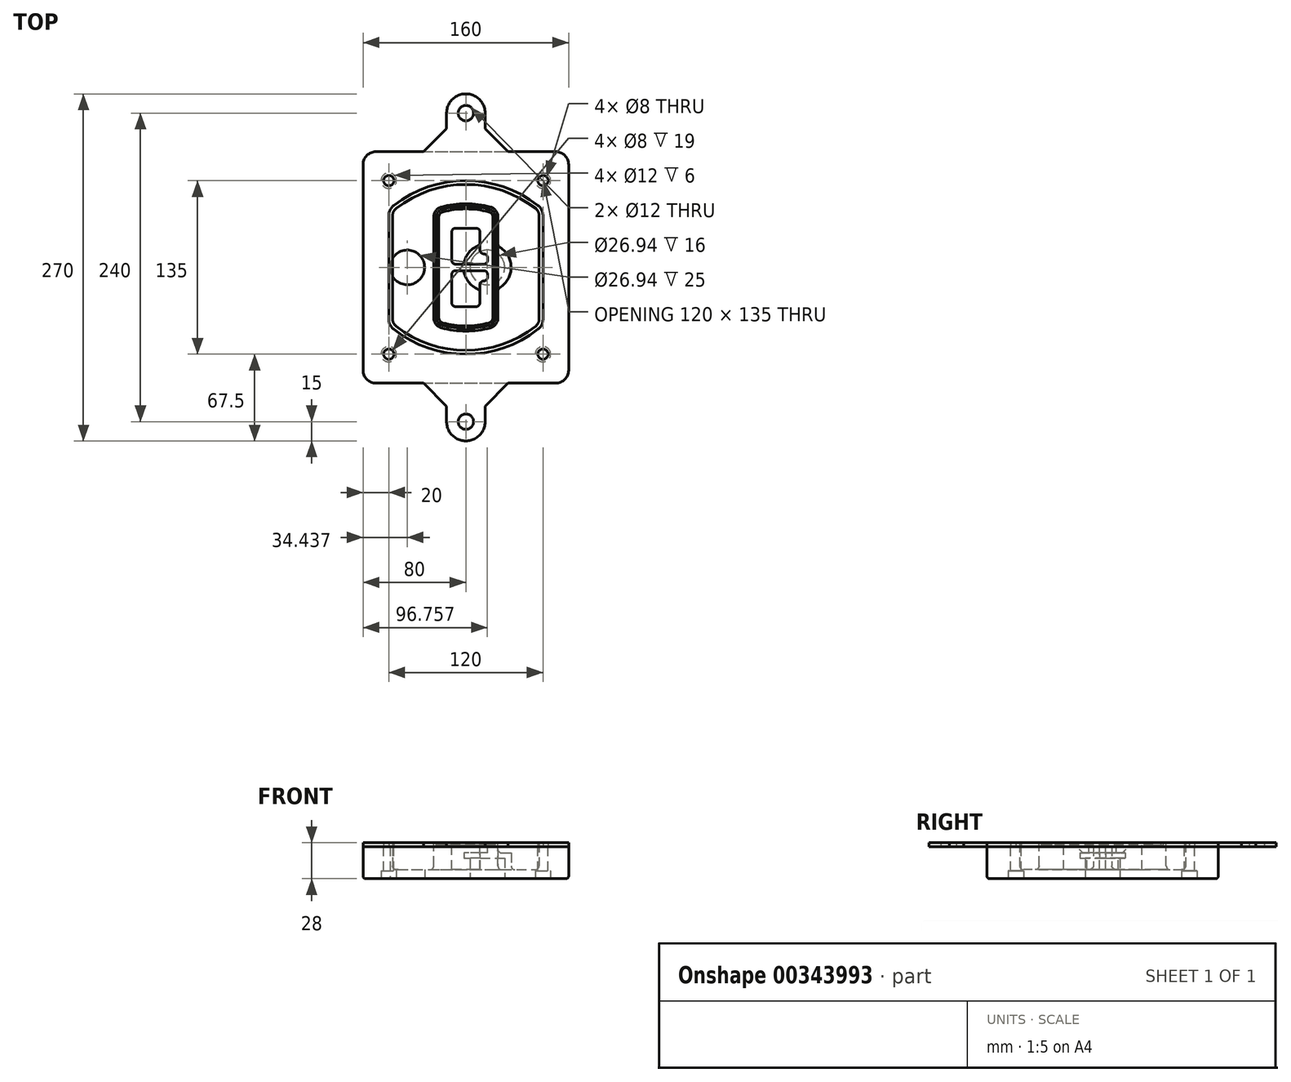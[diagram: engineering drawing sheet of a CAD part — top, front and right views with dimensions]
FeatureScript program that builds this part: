
annotation { "Feature Type Name" : "Feature", "Feature Type Description" : "" }
export const myFeature = defineFeature(function(context is Context, id is Id, definition is map)
    precondition{}
    {
        {
            var Q0;
            Q0=qCreatedBy(makeId("Top.planeOp"),FACE);
            var sketch = newSketch(context, id + "F0", { "sketchPlane" : qUnion([Q0])});
            skPoint(sketch, "E0.rect.middle", {"position": v(0, 0) * mm});
            skLineSegment(sketch, "E1.bottom", {"start": v(-70, -90) * mm, "end": v(70, -90) * mm});
            skLineSegment(sketch, "E1.top", {"start": v(-70, 90) * mm, "end": v(70, 90) * mm});
            skLineSegment(sketch, "E1.left", {"start": v(-80, -80) * mm, "end": v(-80, 80) * mm});
            skLineSegment(sketch, "E1.right", {"start": v(80, -80) * mm, "end": v(80, 80) * mm});
            skLineSegment(sketch, "E2", {"start": v(-80, 90) * mm, "end": v(80, -90) * mm, "construction": true});
            skLineSegment(sketch, "E3", {"start": v(80, 90) * mm, "end": v(-80, -90) * mm, "construction": true});
            skCircle(sketch, "E4", {"center": v(-60, 67.5) * mm, "radius": 4 * mm});
            skCircle(sketch, "E5", {"center": v(60, 67.5) * mm, "radius": 4 * mm});
            skCircle(sketch, "E6", {"center": v(60, -67.5) * mm, "radius": 4 * mm});
            skCircle(sketch, "E7", {"center": v(-60, -67.5) * mm, "radius": 4 * mm});
            skLineSegment(sketch, "E8", {"start": v(-60, 67.5) * mm, "end": v(60, 67.5) * mm, "construction": true});
            skLineSegment(sketch, "E9", {"start": v(60, 67.5) * mm, "end": v(60, -67.5) * mm, "construction": true});
            skLineSegment(sketch, "E10", {"start": v(60, -67.5) * mm, "end": v(-60, -67.5) * mm, "construction": true});
            skLineSegment(sketch, "E11", {"start": v(-60, -67.5) * mm, "end": v(-60, 67.5) * mm, "construction": true});
            skLineSegment(sketch, "E12", {"start": v(-60, 40.3) * mm, "end": v(-60, -40.3) * mm});
            skLineSegment(sketch, "E13", {"start": v(60, 40.3) * mm, "end": v(60, -40.3) * mm});
            skArc(sketch, "E14", {"start": v(56.15, 48.18) * mm, "mid": v(0, 67.5) * mm, "end": v(-56.15, 48.18) * mm});
            skArc(sketch, "E15", {"start": v(-56.15, -48.18) * mm, "mid": v(0, -67.5) * mm, "end": v(56.15, -48.18) * mm});
            skLineSegment(sketch, "E16", {"start": v(-60, 0) * mm, "end": v(60, 0) * mm, "construction": true});
            skPoint(sketch, "E17.visualSharp", {"position": v(-60, -45) * mm});
            skArc(sketch, "E17.filletArc", {"start": v(-60, -40.3) * mm, "mid": v(-58.99, -44.68) * mm, "end": v(-56.15, -48.18) * mm});
            skPoint(sketch, "E18.visualSharp", {"position": v(-60, 45) * mm});
            skArc(sketch, "E18.filletArc", {"start": v(-56.15, 48.18) * mm, "mid": v(-58.99, 44.68) * mm, "end": v(-60, 40.3) * mm});
            skPoint(sketch, "E19.visualSharp", {"position": v(60, 45) * mm});
            skArc(sketch, "E19.filletArc", {"start": v(60, 40.3) * mm, "mid": v(58.99, 44.68) * mm, "end": v(56.15, 48.18) * mm});
            skPoint(sketch, "E20.visualSharp", {"position": v(60, -45) * mm});
            skArc(sketch, "E20.filletArc", {"start": v(56.15, -48.18) * mm, "mid": v(58.99, -44.68) * mm, "end": v(60, -40.3) * mm});
            skPoint(sketch, "E21.visualSharp", {"position": v(-80, 90) * mm});
            skArc(sketch, "E21.filletArc", {"start": v(-70, 90) * mm, "mid": v(-77.07, 87.07) * mm, "end": v(-80, 80) * mm});
            skPoint(sketch, "E22.visualSharp", {"position": v(80, 90) * mm});
            skArc(sketch, "E22.filletArc", {"start": v(80, 80) * mm, "mid": v(77.07, 87.07) * mm, "end": v(70, 90) * mm});
            skPoint(sketch, "E23.visualSharp", {"position": v(80, -90) * mm});
            skArc(sketch, "E23.filletArc", {"start": v(70, -90) * mm, "mid": v(77.07, -87.07) * mm, "end": v(80, -80) * mm});
            skPoint(sketch, "E24.visualSharp", {"position": v(-80, -90) * mm});
            skArc(sketch, "E24.filletArc", {"start": v(-80, -80) * mm, "mid": v(-77.07, -87.07) * mm, "end": v(-70, -90) * mm});
            skArc(sketch, "E25.0", {"start": v(57, 40.3) * mm, "mid": v(56.3, 43.36) * mm, "end": v(54.3, 45.81) * mm});
            skLineSegment(sketch, "E25.1", {"start": v(57, 40.3) * mm, "end": v(57, -40.3) * mm});
            skArc(sketch, "E25.2", {"start": v(54.3, -45.81) * mm, "mid": v(56.3, -43.36) * mm, "end": v(57, -40.3) * mm});
            skArc(sketch, "E25.3", {"start": v(-54.3, -45.81) * mm, "mid": v(0, -64.5) * mm, "end": v(54.3, -45.81) * mm});
            skArc(sketch, "E25.4", {"start": v(-57, -40.3) * mm, "mid": v(-56.3, -43.36) * mm, "end": v(-54.3, -45.81) * mm});
            skArc(sketch, "E25.5", {"start": v(54.3, 45.81) * mm, "mid": v(0, 64.5) * mm, "end": v(-54.3, 45.81) * mm});
            skLineSegment(sketch, "E25.6", {"start": v(-57, 40.3) * mm, "end": v(-57, -40.3) * mm});
            skArc(sketch, "E25.7", {"start": v(-54.3, 45.81) * mm, "mid": v(-56.3, 43.36) * mm, "end": v(-57, 40.3) * mm});
            skArc(sketch, "E26.0", {"start": v(-58.62, 51.33) * mm, "mid": v(-62.58, 46.43) * mm, "end": v(-64, 40.3) * mm});
            skArc(sketch, "E26.1", {"start": v(58.62, 51.33) * mm, "mid": v(0, 71.5) * mm, "end": v(-58.62, 51.33) * mm});
            skArc(sketch, "E26.2", {"start": v(64, 40.3) * mm, "mid": v(62.58, 46.43) * mm, "end": v(58.62, 51.33) * mm});
            skLineSegment(sketch, "E26.3", {"start": v(64, 40.3) * mm, "end": v(64, -40.3) * mm});
            skArc(sketch, "E26.4", {"start": v(58.62, -51.33) * mm, "mid": v(62.58, -46.43) * mm, "end": v(64, -40.3) * mm});
            skLineSegment(sketch, "E26.5", {"start": v(-64, 40.3) * mm, "end": v(-64, -40.3) * mm});
            skArc(sketch, "E26.6", {"start": v(-58.62, -51.33) * mm, "mid": v(0, -71.5) * mm, "end": v(58.62, -51.33) * mm});
            skArc(sketch, "E26.7", {"start": v(-64, -40.3) * mm, "mid": v(-62.58, -46.43) * mm, "end": v(-58.62, -51.33) * mm});
            skSolve(sketch);
        }
        {
            var Q0;
            Q0=makeQuery(id+"F0.imprint","IMPRINT",FACE,{"disambiguationData":[TD([[makeQuery(id+"F0.imprint","IMPRINT",EDGE,{"derivedFrom":sQuery(id+"F0.wireOp",EDGE,"E1.bottom")}),1.0]])]});
            var Q1;
            Q1=makeQuery(id+"F0.imprint","IMPRINT",FACE,{"disambiguationData":[TD([[makeQuery(id+"F0.imprint","IMPRINT",EDGE,{"derivedFrom":sQuery(id+"F0.wireOp",EDGE,"E12")}),1.0]])]});
            var Q2;
            Q2=makeQuery(id+"F0.imprint","IMPRINT",FACE,{"disambiguationData":[TD([[makeQuery(id+"F0.imprint","IMPRINT",EDGE,{"derivedFrom":sQuery(id+"F0.wireOp",EDGE,"E25.0")}),1.0]])]});
            var Q3;
            Q3=makeQuery(id+"F0.imprint","IMPRINT",FACE,{"disambiguationData":[TD([[makeQuery(id+"F0.imprint","IMPRINT",EDGE,{"derivedFrom":sQuery(id+"F0.wireOp",EDGE,"E12")}),-1.0]])]});
            extrude(context, id + "F1", {"entities" : qUnion([Q0, Q1, Q2, Q3]), "oppositeDirection" : true, "depth" : 25 * mm});
        }
        {
            var Q0;
            Q0=makeQuery(id+"F0.imprint","IMPRINT",FACE,{"disambiguationData":[TD([[makeQuery(id+"F0.imprint","IMPRINT",EDGE,{"derivedFrom":sQuery(id+"F0.wireOp",EDGE,"E12")}),1.0]])]});
            extrude(context, id + "F2", {"entities" : qUnion([Q0]), "operationType" : NewBodyOperationType.ADD, "depth" : 3 * mm});
        }
        {
            var Q0;
            Q0=makeQuery(id+"F0.imprint","IMPRINT",FACE,{"disambiguationData":[TD([[makeQuery(id+"F0.imprint","IMPRINT",EDGE,{"derivedFrom":sQuery(id+"F0.wireOp",EDGE,"E25.0")}),1.0]])]});
            extrude(context, id + "F3", {"entities" : qUnion([Q0]), "operationType" : NewBodyOperationType.REMOVE, "oppositeDirection" : true, "depth" : 18 * mm});
        }
        {
            var Q0;
            Q0=makeQuery(id+"F2.opExtrude","CAP_FACE",FACE,{"disambiguationData":[OSD([sQuery(id+"F0.wireOp",EDGE,"E12"),sQuery(id+"F0.wireOp",EDGE,"E13"),sQuery(id+"F0.wireOp",EDGE,"E14"),sQuery(id+"F0.wireOp",EDGE,"E15"),sQuery(id+"F0.wireOp",EDGE,"E17.filletArc"),sQuery(id+"F0.wireOp",EDGE,"E18.filletArc"),sQuery(id+"F0.wireOp",EDGE,"E19.filletArc"),sQuery(id+"F0.wireOp",EDGE,"E20.filletArc"),sQuery(id+"F0.wireOp",EDGE,"E25.0"),sQuery(id+"F0.wireOp",EDGE,"E25.1"),sQuery(id+"F0.wireOp",EDGE,"E25.2"),sQuery(id+"F0.wireOp",EDGE,"E25.3"),sQuery(id+"F0.wireOp",EDGE,"E25.4"),sQuery(id+"F0.wireOp",EDGE,"E25.5"),sQuery(id+"F0.wireOp",EDGE,"E25.6"),sQuery(id+"F0.wireOp",EDGE,"E25.7")])],"isStart":false});
            var sketch = newSketch(context, id + "F4", { "sketchPlane" : qUnion([Q0])});
            skArc(sketch, "E27.0", {"start": v(-19.08, -46.97) * mm, "mid": v(0, -49.5) * mm, "end": v(19.08, -46.97) * mm});
            skArc(sketch, "E28.0", {"start": v(19.08, 46.97) * mm, "mid": v(0, 49.5) * mm, "end": v(-19.08, 46.97) * mm});
            skLineSegment(sketch, "E29", {"start": v(-25, 39.25) * mm, "end": v(-25, -39.25) * mm});
            skLineSegment(sketch, "E30", {"start": v(25, 39.25) * mm, "end": v(25, -39.25) * mm});
            skLineSegment(sketch, "E31", {"start": v(-25, 45.1) * mm, "end": v(25, 45.1) * mm, "construction": true});
            skLineSegment(sketch, "E32", {"start": v(-25, -45.1) * mm, "end": v(25, -45.1) * mm, "construction": true});
            skPoint(sketch, "E33.visualSharp", {"position": v(-25, 45.1) * mm});
            skArc(sketch, "E33.filletArc", {"start": v(-19.08, 46.97) * mm, "mid": v(-23.35, 44.11) * mm, "end": v(-25, 39.25) * mm});
            skPoint(sketch, "E34.visualSharp", {"position": v(25, 45.1) * mm});
            skArc(sketch, "E34.filletArc", {"start": v(25, 39.25) * mm, "mid": v(23.35, 44.11) * mm, "end": v(19.08, 46.97) * mm});
            skPoint(sketch, "E35.visualSharp", {"position": v(25, -45.1) * mm});
            skArc(sketch, "E35.filletArc", {"start": v(19.08, -46.97) * mm, "mid": v(23.35, -44.11) * mm, "end": v(25, -39.25) * mm});
            skPoint(sketch, "E36.visualSharp", {"position": v(-25, -45.1) * mm});
            skArc(sketch, "E36.filletArc", {"start": v(-25, -39.25) * mm, "mid": v(-23.35, -44.11) * mm, "end": v(-19.08, -46.97) * mm});
            skArc(sketch, "E37.0", {"start": v(54.3, 45.81) * mm, "mid": v(0, 64.5) * mm, "end": v(-54.3, 45.81) * mm});
            skArc(sketch, "E37.1", {"start": v(-54.3, 45.81) * mm, "mid": v(-56.3, 43.36) * mm, "end": v(-57, 40.3) * mm});
            skLineSegment(sketch, "E37.2", {"start": v(-57, 40.3) * mm, "end": v(-57, -40.3) * mm});
            skArc(sketch, "E37.3", {"start": v(-57, -40.3) * mm, "mid": v(-56.3, -43.36) * mm, "end": v(-54.3, -45.81) * mm});
            skArc(sketch, "E37.4", {"start": v(-54.3, -45.81) * mm, "mid": v(0, -64.5) * mm, "end": v(54.3, -45.81) * mm});
            skArc(sketch, "E37.5", {"start": v(54.3, -45.81) * mm, "mid": v(56.3, -43.36) * mm, "end": v(57, -40.3) * mm});
            skLineSegment(sketch, "E37.6", {"start": v(57, 40.3) * mm, "end": v(57, -40.3) * mm});
            skArc(sketch, "E37.7", {"start": v(57, 40.3) * mm, "mid": v(56.3, 43.36) * mm, "end": v(54.3, 45.81) * mm});
            skLineSegment(sketch, "E38.0", {"start": v(23, 39.25) * mm, "end": v(23, -39.25) * mm});
            skArc(sketch, "E38.1", {"start": v(18.56, -45.04) * mm, "mid": v(21.76, -42.9) * mm, "end": v(23, -39.25) * mm});
            skArc(sketch, "E38.2", {"start": v(-18.56, -45.04) * mm, "mid": v(0, -47.5) * mm, "end": v(18.56, -45.04) * mm});
            skArc(sketch, "E38.3", {"start": v(-23, -39.25) * mm, "mid": v(-21.76, -42.9) * mm, "end": v(-18.56, -45.04) * mm});
            skLineSegment(sketch, "E38.4", {"start": v(-23, 39.25) * mm, "end": v(-23, -39.25) * mm});
            skArc(sketch, "E38.5", {"start": v(23, 39.25) * mm, "mid": v(21.76, 42.9) * mm, "end": v(18.56, 45.04) * mm});
            skArc(sketch, "E38.6", {"start": v(-18.56, 45.04) * mm, "mid": v(-21.76, 42.9) * mm, "end": v(-23, 39.25) * mm});
            skArc(sketch, "E38.7", {"start": v(18.56, 45.04) * mm, "mid": v(0, 47.5) * mm, "end": v(-18.56, 45.04) * mm});
            skArc(sketch, "E39.0", {"start": v(21, 39.25) * mm, "mid": v(20.18, 41.68) * mm, "end": v(18.04, 43.1) * mm});
            skLineSegment(sketch, "E39.1", {"start": v(21, 39.25) * mm, "end": v(21, -39.25) * mm});
            skArc(sketch, "E39.2", {"start": v(18.04, -43.1) * mm, "mid": v(20.18, -41.68) * mm, "end": v(21, -39.25) * mm});
            skArc(sketch, "E39.3", {"start": v(-18.04, -43.1) * mm, "mid": v(0, -45.5) * mm, "end": v(18.04, -43.1) * mm});
            skArc(sketch, "E39.4", {"start": v(-21, -39.25) * mm, "mid": v(-20.18, -41.68) * mm, "end": v(-18.04, -43.1) * mm});
            skArc(sketch, "E39.5", {"start": v(18.04, 43.1) * mm, "mid": v(0, 45.5) * mm, "end": v(-18.04, 43.1) * mm});
            skLineSegment(sketch, "E39.6", {"start": v(-21, 39.25) * mm, "end": v(-21, -39.25) * mm});
            skArc(sketch, "E39.7", {"start": v(-18.04, 43.1) * mm, "mid": v(-20.18, 41.68) * mm, "end": v(-21, 39.25) * mm});
            skLineSegment(sketch, "E40", {"start": v(-25, 0) * mm, "end": v(25, 0) * mm, "construction": true});
            skLineSegment(sketch, "E41", {"start": v(-11, 5.5) * mm, "end": v(-11, 27.5) * mm});
            skLineSegment(sketch, "E42", {"start": v(-8, 30.5) * mm, "end": v(8, 30.5) * mm});
            skLineSegment(sketch, "E43", {"start": v(11, 27.5) * mm, "end": v(11, 13.5) * mm});
            skLineSegment(sketch, "E44", {"start": v(14, 10.5) * mm, "end": v(14, 10.5) * mm});
            skLineSegment(sketch, "E45", {"start": v(17, 7.5) * mm, "end": v(17, 5.5) * mm});
            skLineSegment(sketch, "E46", {"start": v(14, 2.5) * mm, "end": v(-8, 2.5) * mm});
            skPoint(sketch, "E47.visualSharp", {"position": v(-11, 30.5) * mm});
            skArc(sketch, "E47.filletArc", {"start": v(-8, 30.5) * mm, "mid": v(-10.12, 29.62) * mm, "end": v(-11, 27.5) * mm});
            skPoint(sketch, "E48.visualSharp", {"position": v(11, 30.5) * mm});
            skArc(sketch, "E48.filletArc", {"start": v(11, 27.5) * mm, "mid": v(10.12, 29.62) * mm, "end": v(8, 30.5) * mm});
            skPoint(sketch, "E49.visualSharp", {"position": v(11, 10.5) * mm});
            skArc(sketch, "E49.filletArc", {"start": v(11, 13.5) * mm, "mid": v(11.88, 11.38) * mm, "end": v(14, 10.5) * mm});
            skPoint(sketch, "E50.visualSharp", {"position": v(17, 10.5) * mm});
            skArc(sketch, "E50.filletArc", {"start": v(17, 7.5) * mm, "mid": v(16.12, 9.62) * mm, "end": v(14, 10.5) * mm});
            skPoint(sketch, "E51.visualSharp", {"position": v(17, 2.5) * mm});
            skArc(sketch, "E51.filletArc", {"start": v(14, 2.5) * mm, "mid": v(16.12, 3.38) * mm, "end": v(17, 5.5) * mm});
            skPoint(sketch, "E52.visualSharp", {"position": v(-11, 2.5) * mm});
            skArc(sketch, "E52.filletArc", {"start": v(-11, 5.5) * mm, "mid": v(-10.12, 3.38) * mm, "end": v(-8, 2.5) * mm});
            skLineSegment(sketch, "E53.0.MirrorCS", {"start": v(14, -2.5) * mm, "end": v(-8, -2.5) * mm});
            skArc(sketch, "E54.0.MirrorCS", {"start": v(-11, -5.5) * mm, "mid": v(-10.12, -3.38) * mm, "end": v(-8, -2.5) * mm});
            skLineSegment(sketch, "E55.0.MirrorCS", {"start": v(-11, -5.5) * mm, "end": v(-11, -27.5) * mm});
            skArc(sketch, "E56.0.MirrorCS", {"start": v(-8, -30.5) * mm, "mid": v(-10.12, -29.62) * mm, "end": v(-11, -27.5) * mm});
            skLineSegment(sketch, "E57.0.MirrorCS", {"start": v(-8, -30.5) * mm, "end": v(8, -30.5) * mm});
            skArc(sketch, "E58.0.MirrorCS", {"start": v(11, -27.5) * mm, "mid": v(10.12, -29.62) * mm, "end": v(8, -30.5) * mm});
            skLineSegment(sketch, "E59.0.MirrorCS", {"start": v(11, -27.5) * mm, "end": v(11, -13.5) * mm});
            skArc(sketch, "E60.0.MirrorCS", {"start": v(11, -13.5) * mm, "mid": v(11.88, -11.38) * mm, "end": v(14, -10.5) * mm});
            skArc(sketch, "E61.0.MirrorCS", {"start": v(17, -7.5) * mm, "mid": v(16.12, -9.62) * mm, "end": v(14, -10.5) * mm});
            skLineSegment(sketch, "E62.0.MirrorCS", {"start": v(17, -7.5) * mm, "end": v(17, -5.5) * mm});
            skArc(sketch, "E63.0.MirrorCS", {"start": v(14, -2.5) * mm, "mid": v(16.12, -3.38) * mm, "end": v(17, -5.5) * mm});
            skSolve(sketch);
        }
        {
            var Q0;
            Q0=makeQuery(id+"F4.imprint","IMPRINT",FACE,{"disambiguationData":[TD([[makeQuery(id+"F4.imprint","IMPRINT",EDGE,{"derivedFrom":sQuery(id+"F4.wireOp",EDGE,"E27.0")}),1.0]])]});
            var Q1;
            Q1=makeQuery(id+"F4.imprint","IMPRINT",FACE,{"disambiguationData":[TD([[makeQuery(id+"F4.imprint","IMPRINT",EDGE,{"derivedFrom":sQuery(id+"F4.wireOp",EDGE,"E38.0")}),-1.0]])]});
            var Q2;
            Q2=makeQuery(id+"F4.imprint","IMPRINT",FACE,{"disambiguationData":[TD([[makeQuery(id+"F4.imprint","IMPRINT",EDGE,{"derivedFrom":sQuery(id+"F4.wireOp",EDGE,"E39.0")}),1.0]])]});
            extrude(context, id + "F5", {"entities" : qUnion([Q0, Q1, Q2]), "operationType" : NewBodyOperationType.ADD, "endBound" : BoundingType.UP_TO_NEXT, "oppositeDirection" : true, "depth" : 25 * mm});
        }
        {
            var Q0;
            Q0=makeQuery(id+"F4.imprint","IMPRINT",FACE,{"disambiguationData":[TD([[makeQuery(id+"F4.imprint","IMPRINT",EDGE,{"derivedFrom":sQuery(id+"F4.wireOp",EDGE,"E38.0")}),-1.0]])]});
            extrude(context, id + "F6", {"entities" : qUnion([Q0]), "operationType" : NewBodyOperationType.REMOVE, "oppositeDirection" : true, "depth" : 2 * mm});
        }
        {
            var Q0;
            Q0=makeQuery(id+"F1.opExtrude","CAP_FACE",FACE,{"disambiguationData":[OSD([sQuery(id+"F0.wireOp",EDGE,"E1.bottom"),sQuery(id+"F0.wireOp",EDGE,"E1.top"),sQuery(id+"F0.wireOp",EDGE,"E1.left"),sQuery(id+"F0.wireOp",EDGE,"E1.right"),sQuery(id+"F0.wireOp",EDGE,"E4"),sQuery(id+"F0.wireOp",EDGE,"E5"),sQuery(id+"F0.wireOp",EDGE,"E6"),sQuery(id+"F0.wireOp",EDGE,"E7"),sQuery(id+"F0.wireOp",EDGE,"E21.filletArc"),sQuery(id+"F0.wireOp",EDGE,"E22.filletArc"),sQuery(id+"F0.wireOp",EDGE,"E23.filletArc"),sQuery(id+"F0.wireOp",EDGE,"E24.filletArc")])],"isStart":false});
            var sketch = newSketch(context, id + "F7", { "sketchPlane" : qUnion([Q0])});
            skCircle(sketch, "E64", {"center": v(16.76, 0) * mm, "radius": 13.47 * mm});
            skCircle(sketch, "E65", {"center": v(-45.56, 0) * mm, "radius": 13.47 * mm});
            skLineSegment(sketch, "E66", {"start": v(80, 0) * mm, "end": v(-80, 0) * mm});
            skCircle(sketch, "E67", {"center": v(16.76, 0) * mm, "radius": 18.47 * mm});
            skCircle(sketch, "E68", {"center": v(60, -67.5) * mm, "radius": 6 * mm});
            skCircle(sketch, "E69", {"center": v(-60, -67.5) * mm, "radius": 6 * mm});
            skCircle(sketch, "E70", {"center": v(-60, 67.5) * mm, "radius": 6 * mm});
            skCircle(sketch, "E71", {"center": v(60, 67.5) * mm, "radius": 6 * mm});
            skSolve(sketch);
        }
        {
            var Q0;
            {var subQ1=sQuery(id+"F7.wireOp",EDGE,"E66");var subQ4=sQuery(id+"F7.wireOp",EDGE,"E64");var subQ6=makeQuery(id+"F7.imprint","INTERSECT",VERTEX,{"disambiguationData":[OD(0.0)],"derivedFrom":[subQ4,subQ1]});Q0=makeQuery(id+"F7.imprint","IMPRINT",FACE,{"disambiguationData":[TD([[makeQuery(id+"F7.imprint","IMPRINT",EDGE,{"disambiguationData":[TD([[subQ6,-1.0]])],"derivedFrom":subQ4}),-1.0]])]});}
            var Q1;
            {var subQ0=sQuery(id+"F7.wireOp",EDGE,"E66");var subQ1=sQuery(id+"F7.wireOp",EDGE,"E64");var subQ3=makeQuery(id+"F7.imprint","INTERSECT",VERTEX,{"disambiguationData":[OD(0.0)],"derivedFrom":[subQ1,subQ0]});Q1=makeQuery(id+"F7.imprint","IMPRINT",FACE,{"disambiguationData":[TD([[makeQuery(id+"F7.imprint","IMPRINT",EDGE,{"disambiguationData":[TD([[subQ3,-1.0]])],"derivedFrom":subQ1}),1.0]])]});}
            var Q2;
            {var subQ0=sQuery(id+"F7.wireOp",EDGE,"E66");var subQ1=sQuery(id+"F7.wireOp",EDGE,"E64");var subQ3=makeQuery(id+"F7.imprint","INTERSECT",VERTEX,{"disambiguationData":[OD(0.0)],"derivedFrom":[subQ1,subQ0]});Q2=makeQuery(id+"F7.imprint","IMPRINT",FACE,{"disambiguationData":[TD([[makeQuery(id+"F7.imprint","IMPRINT",EDGE,{"disambiguationData":[TD([[subQ3,1.0]])],"derivedFrom":subQ1}),1.0]])]});}
            var Q3;
            {var subQ1=sQuery(id+"F7.wireOp",EDGE,"E66");var subQ4=sQuery(id+"F7.wireOp",EDGE,"E64");var subQ6=makeQuery(id+"F7.imprint","INTERSECT",VERTEX,{"disambiguationData":[OD(0.0)],"derivedFrom":[subQ4,subQ1]});Q3=makeQuery(id+"F7.imprint","IMPRINT",FACE,{"disambiguationData":[TD([[makeQuery(id+"F7.imprint","IMPRINT",EDGE,{"disambiguationData":[TD([[subQ6,1.0]])],"derivedFrom":subQ4}),-1.0]])]});}
            extrude(context, id + "F8", {"entities" : qUnion([Q0, Q1, Q2, Q3]), "operationType" : NewBodyOperationType.ADD, "oppositeDirection" : true, "depth" : 20 * mm});
        }
        {
            var Q0;
            {var subQ0=sQuery(id+"F7.wireOp",EDGE,"E66");var subQ1=sQuery(id+"F7.wireOp",EDGE,"E64");var subQ3=makeQuery(id+"F7.imprint","INTERSECT",VERTEX,{"disambiguationData":[OD(0.0)],"derivedFrom":[subQ1,subQ0]});Q0=makeQuery(id+"F7.imprint","IMPRINT",FACE,{"disambiguationData":[TD([[makeQuery(id+"F7.imprint","IMPRINT",EDGE,{"disambiguationData":[TD([[subQ3,-1.0]])],"derivedFrom":subQ1}),1.0]])]});}
            var Q1;
            {var subQ0=sQuery(id+"F7.wireOp",EDGE,"E66");var subQ1=sQuery(id+"F7.wireOp",EDGE,"E64");var subQ3=makeQuery(id+"F7.imprint","INTERSECT",VERTEX,{"disambiguationData":[OD(0.0)],"derivedFrom":[subQ1,subQ0]});Q1=makeQuery(id+"F7.imprint","IMPRINT",FACE,{"disambiguationData":[TD([[makeQuery(id+"F7.imprint","IMPRINT",EDGE,{"disambiguationData":[TD([[subQ3,1.0]])],"derivedFrom":subQ1}),1.0]])]});}
            extrude(context, id + "F9", {"entities" : qUnion([Q0, Q1]), "operationType" : NewBodyOperationType.REMOVE, "oppositeDirection" : true, "depth" : 16 * mm});
        }
        {
            var Q0;
            {var subQ0=sQuery(id+"F7.wireOp",EDGE,"E66");var subQ1=sQuery(id+"F7.wireOp",EDGE,"E65");var subQ3=makeQuery(id+"F7.imprint","INTERSECT",VERTEX,{"disambiguationData":[OD(0.0)],"derivedFrom":[subQ1,subQ0]});Q0=makeQuery(id+"F7.imprint","IMPRINT",FACE,{"disambiguationData":[TD([[makeQuery(id+"F7.imprint","IMPRINT",EDGE,{"disambiguationData":[TD([[subQ3,-1.0]])],"derivedFrom":subQ1}),1.0]])]});}
            var Q1;
            {var subQ0=sQuery(id+"F7.wireOp",EDGE,"E66");var subQ1=sQuery(id+"F7.wireOp",EDGE,"E65");var subQ3=makeQuery(id+"F7.imprint","INTERSECT",VERTEX,{"disambiguationData":[OD(0.0)],"derivedFrom":[subQ1,subQ0]});Q1=makeQuery(id+"F7.imprint","IMPRINT",FACE,{"disambiguationData":[TD([[makeQuery(id+"F7.imprint","IMPRINT",EDGE,{"disambiguationData":[TD([[subQ3,1.0]])],"derivedFrom":subQ1}),1.0]])]});}
            extrude(context, id + "F10", {"entities" : qUnion([Q0, Q1]), "operationType" : NewBodyOperationType.REMOVE, "oppositeDirection" : true, "depth" : 25 * mm});
        }
        {
            var Q0;
            Q0=makeQuery(id+"F7.imprint","IMPRINT",FACE,{"disambiguationData":[TD([[makeQuery(id+"F7.imprint","IMPRINT",EDGE,{"derivedFrom":sQuery(id+"F7.wireOp",EDGE,"E68")}),1.0]])]});
            var Q1;
            Q1=makeQuery(id+"F7.imprint","IMPRINT",FACE,{"disambiguationData":[TD([[makeQuery(id+"F7.imprint","IMPRINT",EDGE,{"derivedFrom":makeQuery(id+"F1.opExtrude","CAP_EDGE",EDGE,{"disambiguationData":[OSD([sQuery(id+"F0.wireOp",EDGE,"E5")])],"isStart":false})}),-1.0]])]});
            var Q2;
            Q2=makeQuery(id+"F7.imprint","IMPRINT",FACE,{"disambiguationData":[TD([[makeQuery(id+"F7.imprint","IMPRINT",EDGE,{"derivedFrom":sQuery(id+"F7.wireOp",EDGE,"E69")}),1.0]])]});
            var Q3;
            Q3=makeQuery(id+"F7.imprint","IMPRINT",FACE,{"disambiguationData":[TD([[makeQuery(id+"F7.imprint","IMPRINT",EDGE,{"derivedFrom":makeQuery(id+"F1.opExtrude","CAP_EDGE",EDGE,{"disambiguationData":[OSD([sQuery(id+"F0.wireOp",EDGE,"E4")])],"isStart":false})}),-1.0]])]});
            var Q4;
            Q4=makeQuery(id+"F7.imprint","IMPRINT",FACE,{"disambiguationData":[TD([[makeQuery(id+"F7.imprint","IMPRINT",EDGE,{"derivedFrom":sQuery(id+"F7.wireOp",EDGE,"E70")}),1.0]])]});
            var Q5;
            Q5=makeQuery(id+"F7.imprint","IMPRINT",FACE,{"disambiguationData":[TD([[makeQuery(id+"F7.imprint","IMPRINT",EDGE,{"derivedFrom":makeQuery(id+"F1.opExtrude","CAP_EDGE",EDGE,{"disambiguationData":[OSD([sQuery(id+"F0.wireOp",EDGE,"E7")])],"isStart":false})}),-1.0]])]});
            var Q6;
            Q6=makeQuery(id+"F7.imprint","IMPRINT",FACE,{"disambiguationData":[TD([[makeQuery(id+"F7.imprint","IMPRINT",EDGE,{"derivedFrom":sQuery(id+"F7.wireOp",EDGE,"E71")}),1.0]])]});
            var Q7;
            Q7=makeQuery(id+"F7.imprint","IMPRINT",FACE,{"disambiguationData":[TD([[makeQuery(id+"F7.imprint","IMPRINT",EDGE,{"derivedFrom":makeQuery(id+"F1.opExtrude","CAP_EDGE",EDGE,{"disambiguationData":[OSD([sQuery(id+"F0.wireOp",EDGE,"E6")])],"isStart":false})}),-1.0]])]});
            extrude(context, id + "F11", {"entities" : qUnion([Q0, Q1, Q2, Q3, Q4, Q5, Q6, Q7]), "operationType" : NewBodyOperationType.REMOVE, "oppositeDirection" : true, "depth" : 6 * mm});
        }
        {
            var Q0;
            Q0=makeQuery(id+"F9.boolean.opBoolean","COPY",FACE,{"derivedFrom":makeQuery(id+"F9.opExtrude","CAP_FACE",FACE,{"disambiguationData":[OSD([sQuery(id+"F7.wireOp",EDGE,"E64")])],"isStart":false})});
            var sketch = newSketch(context, id + "F12", { "sketchPlane" : qUnion([Q0])});
            skArc(sketch, "E72.0", {"start": v(11, 17.55) * mm, "mid": v(2.57, 11.82) * mm, "end": v(-1.54, 2.5) * mm});
            skArc(sketch, "E72.1", {"start": v(-1.54, -2.5) * mm, "mid": v(2.57, -11.82) * mm, "end": v(11, -17.55) * mm});
            skLineSegment(sketch, "E73", {"start": v(-1.54, -2.5) * mm, "end": v(14, -2.5) * mm});
            skLineSegment(sketch, "E74.0", {"start": v(14, 2.5) * mm, "end": v(-1.54, 2.5) * mm});
            skArc(sketch, "E74.1", {"start": v(14, 2.5) * mm, "mid": v(16.12, 3.38) * mm, "end": v(17, 5.5) * mm});
            skLineSegment(sketch, "E74.2", {"start": v(17, 7.5) * mm, "end": v(17, 5.5) * mm});
            skArc(sketch, "E74.3", {"start": v(17, 7.5) * mm, "mid": v(16.12, 9.62) * mm, "end": v(14, 10.5) * mm});
            skArc(sketch, "E74.4", {"start": v(11, 13.5) * mm, "mid": v(11.88, 11.38) * mm, "end": v(14, 10.5) * mm});
            skLineSegment(sketch, "E74.5", {"start": v(11, 17.55) * mm, "end": v(11, 13.5) * mm});
            skLineSegment(sketch, "E74.7", {"start": v(14, -2.5) * mm, "end": v(-1.54, -2.5) * mm});
            skArc(sketch, "E74.8", {"start": v(14, -2.5) * mm, "mid": v(16.12, -3.38) * mm, "end": v(17, -5.5) * mm});
            skLineSegment(sketch, "E74.9", {"start": v(17, -7.5) * mm, "end": v(17, -5.5) * mm});
            skArc(sketch, "E74.10", {"start": v(17, -7.5) * mm, "mid": v(16.12, -9.62) * mm, "end": v(14, -10.5) * mm});
            skArc(sketch, "E74.11", {"start": v(11, -13.5) * mm, "mid": v(11.88, -11.38) * mm, "end": v(14, -10.5) * mm});
            skLineSegment(sketch, "E74.12", {"start": v(11, -17.55) * mm, "end": v(11, -13.5) * mm});
            skPoint(sketch, "E75.orphan", {"position": v(11, -27.5) * mm});
            skPoint(sketch, "E76.orphan", {"position": v(-8, -2.5) * mm});
            skPoint(sketch, "E77.orphan", {"position": v(-8, 2.5) * mm});
            skPoint(sketch, "E78.orphan", {"position": v(11, 27.5) * mm});
            skSolve(sketch);
        }
        {
            var Q0;
            {var subQ7=sQuery(id+"F12.wireOp",EDGE,"E72.0");var subQ14=sQuery(id+"F12.wireOp",EDGE,"E72.1");var subQ16=sQuery(id+"F12.wireOp",EDGE,"E74.1");var subQ18=sQuery(id+"F12.wireOp",EDGE,"E74.8");Q0=qUnion([makeQuery(id+"F12.imprint","IMPRINT",FACE,{"disambiguationData":[TD([[makeQuery(id+"F12.imprint","IMPRINT",EDGE,{"derivedFrom":subQ7}),1.0]])]}),makeQuery(id+"F12.imprint","IMPRINT",FACE,{"disambiguationData":[TD([[makeQuery(id+"F12.imprint","IMPRINT",EDGE,{"derivedFrom":subQ14}),1.0]])]}),makeQuery(id+"F12.imprint","IMPRINT",FACE,{"disambiguationData":[TD([[makeQuery(id+"F12.imprint","IMPRINT",EDGE,{"derivedFrom":subQ16}),1.0]])]}),makeQuery(id+"F12.imprint","IMPRINT",FACE,{"disambiguationData":[TD([[makeQuery(id+"F12.imprint","IMPRINT",EDGE,{"derivedFrom":subQ18}),-1.0]])]})]);}
            var Q1;
            Q1=makeQuery(id+"F5.boolean.opBoolean","SPLIT",FACE,{"disambiguationData":[TD([makeQuery(id+"F5.opExtrude","SWEPT_FACE",FACE,{"disambiguationData":[OSD([sQuery(id+"F4.wireOp",EDGE,"E41")])]})])],"derivedFrom":makeQuery(id+"F3.boolean.opBoolean","COPY",FACE,{"derivedFrom":makeQuery(id+"F3.opExtrude","CAP_FACE",FACE,{"disambiguationData":[OSD([sQuery(id+"F0.wireOp",EDGE,"E25.0"),sQuery(id+"F0.wireOp",EDGE,"E25.1"),sQuery(id+"F0.wireOp",EDGE,"E25.2"),sQuery(id+"F0.wireOp",EDGE,"E25.3"),sQuery(id+"F0.wireOp",EDGE,"E25.4"),sQuery(id+"F0.wireOp",EDGE,"E25.5"),sQuery(id+"F0.wireOp",EDGE,"E25.6"),sQuery(id+"F0.wireOp",EDGE,"E25.7")])],"isStart":false})})});
            extrude(context, id + "F13", {"entities" : qUnion([Q0]), "operationType" : NewBodyOperationType.REMOVE, "endBound" : BoundingType.UP_TO_SURFACE, "endBoundEntityFace" : qUnion([Q1]), "depth" : 25 * mm});
        }
        {
            var Q0;
            Q0=makeQuery(id+"F3.boolean.opBoolean","COPY",EDGE,{"derivedFrom":makeQuery(id+"F3.opExtrude","CAP_EDGE",EDGE,{"disambiguationData":[OSD([sQuery(id+"F0.wireOp",EDGE,"E25.6")])],"isStart":false})});
            var Q1;
            Q1=makeQuery(id+"F8.boolean.opBoolean","INTERSECT",EDGE,{"derivedFrom":[makeQuery(id+"F5.opExtrude","SWEPT_FACE",FACE,{"disambiguationData":[OSD([sQuery(id+"F4.wireOp",EDGE,"E30")])]}),makeQuery(id+"F8.opExtrude","CAP_FACE",FACE,{"disambiguationData":[OSD([sQuery(id+"F7.wireOp",EDGE,"E67")])],"isStart":false})]});
            var Q2;
            Q2=makeQuery(id+"F8.boolean.opBoolean","INTERSECT",EDGE,{"disambiguationData":[OD(1.0)],"derivedFrom":[makeQuery(id+"F5.opExtrude","SWEPT_FACE",FACE,{"disambiguationData":[OSD([sQuery(id+"F4.wireOp",EDGE,"E30")])]}),makeQuery(id+"F8.opExtrude","SWEPT_FACE",FACE,{"disambiguationData":[OSD([sQuery(id+"F7.wireOp",EDGE,"E67")])]})]});
            var Q3;
            {var subQ0=sQuery(id+"F4.wireOp",EDGE,"E30");Q3=makeQuery(id+"F8.boolean.opBoolean","SPLIT",EDGE,{"disambiguationData":[TD([makeQuery(id+"F5.opExtrude","SWEPT_FACE",FACE,{"disambiguationData":[OSD([sQuery(id+"F4.wireOp",EDGE,"E35.filletArc")])]})])],"derivedFrom":makeQuery(id+"F5.opExtrude","CAP_EDGE",EDGE,{"disambiguationData":[OSD([subQ0])],"isStart":false})});}
            var Q4;
            {var subQ0=sQuery(id+"F0.wireOp",EDGE,"E25.7");var subQ1=sQuery(id+"F0.wireOp",EDGE,"E25.1");var subQ2=sQuery(id+"F0.wireOp",EDGE,"E25.6");var subQ3=sQuery(id+"F0.wireOp",EDGE,"E25.5");var subQ4=sQuery(id+"F0.wireOp",EDGE,"E25.4");var subQ5=sQuery(id+"F0.wireOp",EDGE,"E25.0");var subQ6=sQuery(id+"F0.wireOp",EDGE,"E25.2");var subQ7=sQuery(id+"F0.wireOp",EDGE,"E25.3");Q4=makeQuery(id+"F8.boolean.opBoolean","INTERSECT",EDGE,{"derivedFrom":[makeQuery(id+"F5.boolean.opBoolean","SPLIT",FACE,{"disambiguationData":[TD([makeQuery(id+"F2.opExtrude","SWEPT_FACE",FACE,{"disambiguationData":[OSD([subQ5])]})])],"derivedFrom":makeQuery(id+"F3.boolean.opBoolean","COPY",FACE,{"derivedFrom":makeQuery(id+"F3.opExtrude","CAP_FACE",FACE,{"disambiguationData":[OSD([subQ5,subQ1,subQ6,subQ7,subQ4,subQ3,subQ2,subQ0])],"isStart":false})})}),makeQuery(id+"F8.opExtrude","SWEPT_FACE",FACE,{"disambiguationData":[OSD([sQuery(id+"F7.wireOp",EDGE,"E67")])]})]});}
            var Q5;
            Q5=makeQuery(id+"F8.boolean.opBoolean","INTERSECT",EDGE,{"disambiguationData":[OD(0.0)],"derivedFrom":[makeQuery(id+"F5.opExtrude","SWEPT_FACE",FACE,{"disambiguationData":[OSD([sQuery(id+"F4.wireOp",EDGE,"E30")])]}),makeQuery(id+"F8.opExtrude","SWEPT_FACE",FACE,{"disambiguationData":[OSD([sQuery(id+"F7.wireOp",EDGE,"E67")])]})]});
            fillet(context, id + "F14", {"entities" : qUnion([Q0, Q1, Q2, Q3, Q4, Q5]), "radius" : 3 * mm, "tangentPropagation" : true, "allowEdgeOverflow" : false});
        }
        {
            var Q0;
            Q0=makeQuery(id+"F1.opExtrude","CAP_EDGE",EDGE,{"disambiguationData":[OSD([sQuery(id+"F0.wireOp",EDGE,"E1.bottom")])],"isStart":false});
            fillet(context, id + "F15", {"entities" : qUnion([Q0]), "radius" : 2 * mm, "tangentPropagation" : true, "allowEdgeOverflow" : false});
        }
        {
            var Q0;
            {var subQ0=sQuery(id+"F0.wireOp",EDGE,"E21.filletArc");var subQ1=sQuery(id+"F0.wireOp",EDGE,"E7");var subQ2=sQuery(id+"F0.wireOp",EDGE,"E6");var subQ3=sQuery(id+"F0.wireOp",EDGE,"E5");var subQ4=sQuery(id+"F0.wireOp",EDGE,"E4");var subQ5=sQuery(id+"F0.wireOp",EDGE,"E22.filletArc");var subQ6=sQuery(id+"F0.wireOp",EDGE,"E1.bottom");var subQ7=sQuery(id+"F0.wireOp",EDGE,"E1.right");var subQ8=sQuery(id+"F0.wireOp",EDGE,"E1.top");var subQ9=sQuery(id+"F0.wireOp",EDGE,"E1.left");var subQ10=sQuery(id+"F0.wireOp",EDGE,"E23.filletArc");var subQ11=sQuery(id+"F0.wireOp",EDGE,"E24.filletArc");Q0=makeQuery(id+"F2.boolean.opBoolean","SPLIT",FACE,{"disambiguationData":[TD([makeQuery(id+"F1.opExtrude","SWEPT_FACE",FACE,{"disambiguationData":[OSD([subQ6])]})])],"derivedFrom":makeQuery(id+"F1.opExtrude","CAP_FACE",FACE,{"disambiguationData":[OSD([subQ6,subQ8,subQ9,subQ7,subQ4,subQ3,subQ2,subQ1,subQ0,subQ5,subQ10,subQ11])],"isStart":true})});}
            var sketch = newSketch(context, id + "F16", { "sketchPlane" : qUnion([Q0])});
            skCircle(sketch, "E79", {"center": v(0, 120) * mm, "radius": 6 * mm});
            skLineSegment(sketch, "E80", {"start": v(0, 120) * mm, "end": v(0, 90) * mm, "construction": true});
            skArc(sketch, "E81", {"start": v(14.98, 119.26) * mm, "mid": v(0, 135) * mm, "end": v(-14.98, 119.26) * mm});
            skLineSegment(sketch, "E82", {"start": v(-14.98, 119.26) * mm, "end": v(-14.98, 108) * mm});
            skLineSegment(sketch, "E83", {"start": v(14.98, 119.26) * mm, "end": v(14.98, 108) * mm});
            skLineSegment(sketch, "E84", {"start": v(-14.98, 108) * mm, "end": v(-32.98, 90) * mm});
            skLineSegment(sketch, "E85", {"start": v(14.98, 108) * mm, "end": v(32.98, 90) * mm});
            skLineSegment(sketch, "E86", {"start": v(-80, 0) * mm, "end": v(80, 0) * mm, "construction": true});
            skLineSegment(sketch, "E87.MirrorCS", {"start": v(14.98, -108) * mm, "end": v(32.98, -90) * mm});
            skLineSegment(sketch, "E88.MirrorCS", {"start": v(-14.98, -108) * mm, "end": v(-32.98, -90) * mm});
            skLineSegment(sketch, "E89.MirrorCS", {"start": v(-14.98, -119.26) * mm, "end": v(-14.98, -108) * mm});
            skLineSegment(sketch, "E90.MirrorCS", {"start": v(14.98, -119.26) * mm, "end": v(14.98, -108) * mm});
            skArc(sketch, "E91.MirrorCS", {"start": v(14.98, -119.26) * mm, "mid": v(0, -135) * mm, "end": v(-14.98, -119.26) * mm});
            skCircle(sketch, "E92.MirrorC", {"center": v(0, -120) * mm, "radius": 6 * mm});
            skLineSegment(sketch, "E93.MirrorCS", {"start": v(0, -120) * mm, "end": v(0, -90) * mm, "construction": true});
            skSolve(sketch);
        }
        {
            var Q0;
            Q0=makeQuery(id+"F16.imprint","IMPRINT",FACE,{"disambiguationData":[TD([[makeQuery(id+"F16.imprint","IMPRINT",EDGE,{"derivedFrom":sQuery(id+"F16.wireOp",EDGE,"E79")}),-1.0]])]});
            var Q1;
            Q1=makeQuery(id+"F16.imprint","IMPRINT",FACE,{"disambiguationData":[TD([[makeQuery(id+"F16.imprint","IMPRINT",EDGE,{"derivedFrom":makeQuery(id+"F1.opExtrude","CAP_EDGE",EDGE,{"disambiguationData":[OSD([sQuery(id+"F0.wireOp",EDGE,"E1.left")])],"isStart":true})}),-1.0]])]});
            var Q2;
            {var subQ1=sQuery(id+"F16.wireOp",EDGE,"E87.MirrorCS");Q2=makeQuery(id+"F16.imprint","IMPRINT",FACE,{"disambiguationData":[TD([[makeQuery(id+"F16.imprint","IMPRINT",EDGE,{"derivedFrom":subQ1}),1.0]])]});}
            var Q3;
            Q3=makeQuery(id+"F2.opExtrude","CAP_FACE",FACE,{"disambiguationData":[OSD([sQuery(id+"F0.wireOp",EDGE,"E12"),sQuery(id+"F0.wireOp",EDGE,"E13"),sQuery(id+"F0.wireOp",EDGE,"E14"),sQuery(id+"F0.wireOp",EDGE,"E15"),sQuery(id+"F0.wireOp",EDGE,"E17.filletArc"),sQuery(id+"F0.wireOp",EDGE,"E18.filletArc"),sQuery(id+"F0.wireOp",EDGE,"E19.filletArc"),sQuery(id+"F0.wireOp",EDGE,"E20.filletArc"),sQuery(id+"F0.wireOp",EDGE,"E25.0"),sQuery(id+"F0.wireOp",EDGE,"E25.1"),sQuery(id+"F0.wireOp",EDGE,"E25.2"),sQuery(id+"F0.wireOp",EDGE,"E25.3"),sQuery(id+"F0.wireOp",EDGE,"E25.4"),sQuery(id+"F0.wireOp",EDGE,"E25.5"),sQuery(id+"F0.wireOp",EDGE,"E25.6"),sQuery(id+"F0.wireOp",EDGE,"E25.7")])],"isStart":false});
            extrude(context, id + "F17", {"entities" : qUnion([Q0, Q1, Q2]), "endBound" : BoundingType.UP_TO_SURFACE, "endBoundEntityFace" : qUnion([Q3]), "depth" : 25 * mm});
        }
    });
